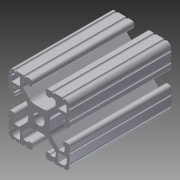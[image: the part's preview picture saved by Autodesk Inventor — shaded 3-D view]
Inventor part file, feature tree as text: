
AUTODESK INVENTOR PART (.ipt)
format: ipt  version: 2013 (Build 170138000, 138)  size: 303,616 bytes
history: native  units: in
note: dims shown in document units (in); Inventor stores cm internally (conversion verified against a paired STEP export)
features: extrude x1, sketch x1
ambient origin geometry x8: Origin, YZ Plane, XZ Plane, XY Plane, X Axis, Y Axis, Z Axis, Center Point
bodies: Solid1 (feature_tree)
feature tree (2):
  extrude  "Extrusion1"  [1 undecoded]
  sketch  "Sketch1"  dims[d0=2.5in d1=0.0in]
note: 1 required parameter value undecoded (feature->parameter linkage not recoverable at this tier; creation-order binding heuristic only, values carry confidence <= 0.55)
